FCSTD DOCUMENT  (FreeCAD 0.20R29603 (Git))
Label: Parameters
License: All rights reserved
LicenseURL: http://en.wikipedia.org/wiki/All_rights_reserved
objects: Spreadsheet::Sheet×2

FEATURE [Spreadsheet::Sheet] Spreadsheet  label="DeskDimensions"
  cells = A1=Desk Parameters; A2=Stock Thickness; B2(Stock_Thickness)==15" / 32; A4=Table Width; B4(Table_Width)==2.5'; A5=Table Length; B5(Table_Length)==4.5'; A7=Leg Length; B7(Leg_Length)==30"; A8=Leg Top; B8(Leg_Top)==4.5"; A9=Leg Bottom; B9(Leg_Bottom)==2"; A11=Skirt Width; B11(Skirt_Width)==Table_Width - 6" - 3 * Stock_Thickness; A12=Skirt Length; B12(Skirt_Length)==Table_Length - 6"; A13=Skirt Height; B13(Skirt_Height)==4"
FEATURE [Spreadsheet::Sheet] BOM  label="Master BOM"
  cells = A1=ModelName; B1=LeafPart; C1=Quantity; D1=Height; E1=Width; F1=Length; G1=SourceFile; A2=Desktop; B2=1; C2=1; D2=11.90625; E2=1371.6; F2=762; G2=<userpath>/Documents/CAD/SimpleDesk/Desktop.FCStd; A3=Leg; B3=1; C3=8; D3=11.90625; E3=762; F3=221.3921159998366; G3=<userpath>/Documents/CAD/SimpleDesk/Leg.FCStd; A4=LongSkirt; B4=1; C4=2; D4=11.90625; E4=1247.757897611526; F4=101.6; G4=<userpath>/Documents/CAD/SimpleDesk/LongSkirt.FCStd; A5=ShortSkirt; B5=1; C5=2; D5=11.90625; E5=573.88125; F5=101.6; G5=<userpath>/Documents/CAD/SimpleDesk/ShortSkirt.FCStd; A6=LegSpacer; B6=1; C6=4; D6=11.90625; E6=50.79999999999995; F6=62.17280773332241; G6=<userpath>/Documents/CAD/SimpleDesk/LegSpacer.FCStd; A7=DeskAssembly; B7=0; C7=1; D7=773.9062500000001; E7=1433.384231999674; F7=762; G7=<userpath>/Documents/CAD/SimpleDesk/DeskAssembly.FCStd
